# Revit family: SIVS-550_G_E
name_source: partatom
category: Mechanical Equipment
revit_build: Autodesk Revit 2014 (Build: 20140709_2115(x64)
units: mm (PartAtom-declared; Revit-internal decimal feet)

## types (1)
- Indirect-Water-Heater_Lochinvar_Ltd-SIVS-550_G_E
    1e Maintenance (check-up) = 3 months after installation
    2nd Maintenance (general maintenance) = 12 months after installation
    Assembly Code = D3010
    BIM Content Developer = CAD & Company
    BIM Content Developer URL = http://www.cadcompany.nl
    Cold Water Connection R = 2 1/2"
    Description = Squire Indirect Water Heater
    Destination / Country = UK & Ireland
    Diameter (with insulation) = 1500 mm  [stored 4.92126 ft]
    Diameter (without insulation) = 1400 mm  [stored 4.59318 ft]
    Draw-off Capacity @ ΔT = 28°C after 120 min. = 10699.0 L
    Draw-off Capacity @ ΔT = 28°C after 30 min. = 4018.0 L
    Draw-off Capacity @ ΔT = 28°C after 60 min. = 6245.0 L
    Draw-off Capacity @ ΔT = 28°C after 90 min. = 8472.0 L
    Draw-off Capacity @ ΔT = 44°C after 120 min. = 6808.0 L
    Draw-off Capacity @ ΔT = 44°C after 30 min. = 2557.0 L
    Draw-off Capacity @ ΔT = 44°C after 60 min. = 3974.0 L
    Draw-off Capacity @ ΔT = 44°C after 90 min. = 5391.0 L
    Draw-off Capacity @ ΔT = 50°C after 120 min. = 5991.0 L
    Draw-off Capacity @ ΔT = 50°C after 30 min. = 2250.0 L
    Draw-off Capacity @ ΔT = 50°C after 60 min. = 3497.0 L
    Draw-off Capacity @ ΔT = 50°C after 90 min. = 4744.0 L
    Draw-off Capacity @ ΔT = 55°C after 120 min. = 5447.0 L
    Draw-off Capacity @ ΔT = 55°C after 30 min. = 2046.0 L
    Draw-off Capacity @ ΔT = 55°C after 60 min. = 3179.0 L
    Draw-off Capacity @ ΔT = 55°C after 90 min. = 4313.0 L
    Draw-off Capacity @ ΔT = 70°C after 120 min. = 4279.0 L
    Draw-off Capacity @ ΔT = 70°C after 30 min. = 1607.0 L
    Draw-off Capacity @ ΔT = 70°C after 60 min. = 2498.0 L
    Draw-off Capacity @ ΔT = 70°C after 90 min. = 3389.0 L
    Empty Weight = 576.00 kg
    Flow Rate - Volume L/h = 6871
    Heating Up Time @ ΔT = 28°C = 14
    Heating Up Time @ ΔT = 44°C = 21
    Heating Up Time @ ΔT = 50°C = 24
    Heating Up Time @ ΔT = 55°C = 27
    Heating Up Time @ ΔT = 70°C = 34
    Height (with insulation) = 1989 mm  [stored 6.52559 ft]
    Height (without insulation) = 1932 mm
    Height Cold Water Inlet = 183 mm
    Height Warm Water Outlet = 1989 mm  [stored 6.52559 ft]
    Hot / Warm Water Connection R = 2 1/2"
    Insulation Thickness = 57 mm  [stored 0.187008 ft]
    Length = 0 mm  [stored 0 ft]
    Maintenance Interval = 12 months
    Manufacturer = Lochinvar Limited
    Manufacturer Number = E 7110
E 7110
E 7110
    Max. Operating Pressure - heat exchanger = 60000.0 Pa
    Max. Operating Pressure - tank = 80000.0 Pa
    Max. Temperature - heat exchanger = 90 °C
    Max. Temperature - tank = 85 °C
    Model = SIVS 550 G E
    Nominal Output - heat exchanger = 159000 W
    Operating Weight = 3126.00 kg
    Packaging Height = 2120 mm
    Packaging Length = 1680 mm
    Packaging Width = 1498 mm
    Pressure Loss - heat exchanger 80ºC/60ºC = 695000.0 Pa
    Product Documentation Link = https://lochinvar.ltd.uk
    Product Instruction Link = https://lochinvar.ltd.uk
    Recovery Rate @ ΔT = 28°C (ltr/hr) = 4454
    Recovery Rate @ ΔT = 44°C (ltr/hr) = 2834
    Recovery Rate @ ΔT = 50°C (ltr/hr) = 2494
    Recovery Rate @ ΔT = 55°C (ltr/hr) = 2267
    Recovery Rate @ ΔT = 70°C (ltr/hr) = 1781
    Serial Number = 8717449269265
    Stand-by Loss = 0 W
    Stand-by Loss - daily (Watt/24H) = 0
    Storage Capacity - heat exchanger = 45 m³
    Storage Capacity - tank = 2600 m³
    Surface Heat Exchanger = 6 m²
    T&P Connection Rp = 1"
    Transport Weight = 686.00 kg
    Type of Packaging = Plastic and Wood
    URL = www.lochinvar.ltd.uk
    Warranty on Parts = 12 months
    Warranty on Tank = 36 months
    Width = 0 mm  [stored 0 ft]
    Workspace = 1250 mm

note: [stored X ft] marks values corroborated as IEEE doubles in the binary element streams (Revit-internal decimal feet)

## geometry (parser evidence)
native form markers: Sweep x19
no freeform markers — native parametric forms only
